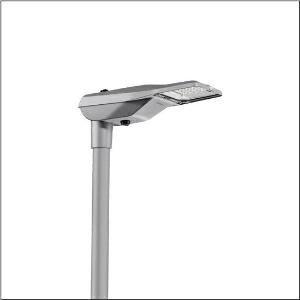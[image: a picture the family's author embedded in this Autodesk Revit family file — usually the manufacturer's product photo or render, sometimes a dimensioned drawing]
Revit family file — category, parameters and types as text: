
# Revit family: streetlight_sl_21_iq_micro___st0_8a_5xe1c31y08db_8273
name_source: partatom
category: Lighting Fixtures
units: mm (PartAtom-declared; Revit-internal decimal feet)

## family parameters
Cut with Voids When Loaded = No
Host = Face
Light Source = No
Part Type = Normal
Room Calculation Point = No
Round Connector Dimension = Use Diameter
Shared = No

## types (1)
- --- (1 x LED, 5110 lm, 39.1 W, 3000K)
    Apparent Load = 39 VA
    CIE Flux Codes = 38 75 97 100 100
    Color Rendering = 70
    Color Temperature = 3000K
    Default Elevation = 1800 mm
    Description = Streetlight SL 21 iQ micro, mast luminaire, primary light control with lens, of PMMA, primary optical cover: cover, of toughened safety glass, transparent, light distribution: ST0.8a, light emission: direct distribution, primary light characteristic: asymmetric, installation type: post-top, side-entry, LED, High Power LED, rated luminous flux: 5.110lm, luminous efficacy: 131lm/W, light colour: 730, colour temperature: 3000K, control: presetting dimming logarithmic, Street-Remote, Auto-Match, Temp-Guard, Lumen-Switch, Night-Set, Smart-Wire, Light-Fading, Desk-Remote (wireless, voltage-free reading and setting of iQ features in the workshop via application-optimized NFC function/RFID function), optimised constant luminous flux control (CLO 2.0), mains connection: 220..240V, AC, 50/60Hz, start of lifetime: 39W, end of service life: 41W, reduction: 17W, luminaire housing, of diecast aluminium, powder-coated, Siteco® metallic grey (DB 702S), corrosivity category C5 mid according to DIN EN ISO 12944, please order mast flange separately, inclination adjustable: 0°, 5°, 10°, 15°, sealing non-destructively replaceable, multi-level sealing system, length: 528mm, width: 235mm, height: 110mm, mast flange for spigot size: 42mm (side-entry): 5XC10008XM4, 60/48mm (side-entry/post-top): 5XC10108XM2, 76/60mm (side-entry/post-top): 5XC10108XM1, Smart Interface below and above, protection rating (complete): IP66, insulation class (complete): insulation class II (safety insulation), certification: CE, ENEC, ENEC+, VDE, impact resistance: IK09, permissible operating ambient temperature for outdoor applications: -40..+50°C, standard-compliant lighting for roads and squares, packaging unit: 1 piece

Light Distribution: ST0.8a
    Height = 110 mm
    Lamp = 1 x LED
    Lamp Light Flux = 5110 lm
    Lamp Power = 39.1 W
    Lamp count = 1
    Length = 528 mm
    Luminous efficacy = 131 lm/W
    Manufacturer = Siteco
    ModVariant = No
    Model = 5XE1C31Y08DB
    Number of Poles = 1
    OnlyDefault = Yes
    Power Factor = 1
    Product Name = Streetlight SL 21 iQ micro | ST0.8a
    Product group = mast luminaire | pylon top
    ProductGroupID = 6100
    Protection Class = Protection class II
    Protection Degree = IP 66
    RLX_Detail_Level = 1
    RLX_Emergency_Light_Flux = 0 lm
    RLX_Emergency_Type = 0
    RLX_Emergency_Type_DB = No
    RlxData = <blob elided: 98561 chars, md5=35052090>
    Socket = socket
    Standby Power = 0 W
    System Light Flux = 5110 lm
    System Power = 39 W
    Type Comments = factory setting: luminous flux: 100 % | dim-lin: 254 | 765 mA
    Type Image = l_1007239.jpg
    URL = http://relux.com
    VarID = @adj_043425
    Voltage = 0 V
    Weight = 0.00 kg
    Width = 235 mm

## geometry (parser evidence)
native form markers: Blend x4, Sweep x10
no freeform markers — native parametric forms only
